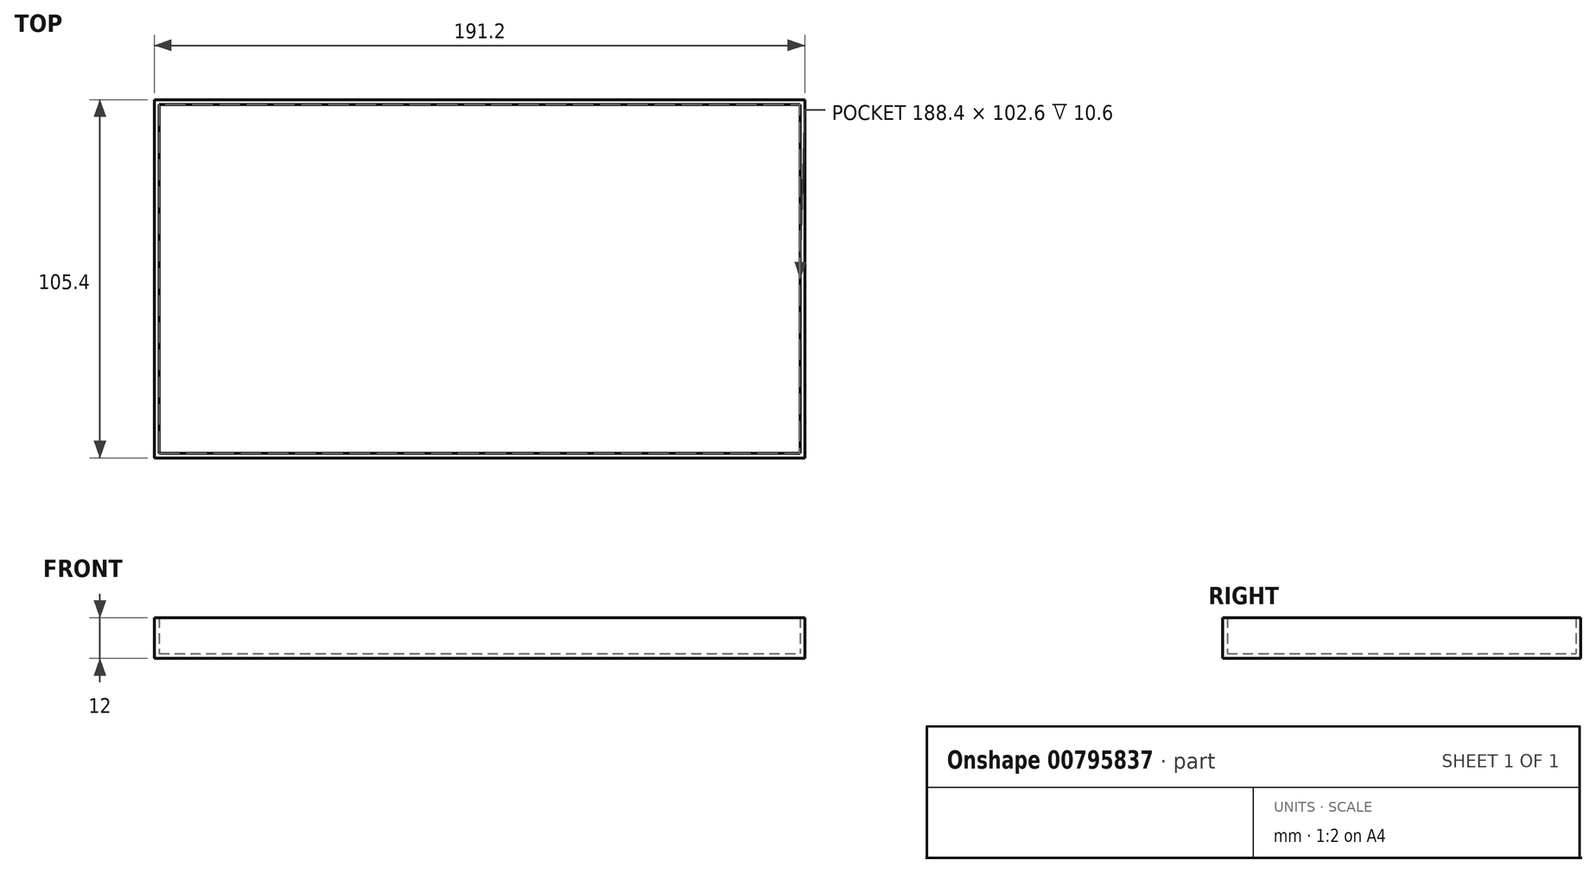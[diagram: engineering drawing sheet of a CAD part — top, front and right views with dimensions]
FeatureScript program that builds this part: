
annotation { "Feature Type Name" : "Feature", "Feature Type Description" : "" }
export const myFeature = defineFeature(function(context is Context, id is Id, definition is map)
    precondition{}
    {
        {
            var Q0;
            Q0=qCreatedBy(makeId("Top.planeOp"),FACE);
            var sketch = newSketch(context, id + "F0", { "sketchPlane" : qUnion([Q0]) });
            skLineSegment(sketch, "E0", {"start": v(-112.85, 61.36) * mm, "end": v(78.35, 61.36) * mm});
            skLineSegment(sketch, "E1", {"start": v(78.35, 61.36) * mm, "end": v(78.35, -44.04) * mm});
            skLineSegment(sketch, "E2", {"start": v(78.35, -44.04) * mm, "end": v(-112.85, -44.04) * mm});
            skLineSegment(sketch, "E3", {"start": v(-112.85, -44.04) * mm, "end": v(-112.85, 61.36) * mm});
            skSolve(sketch);
        }
        {
            var Q0;
            Q0 = qSketchRegion(id + "F0", true);
            extrude(context, id + "F1", {"entities" : qUnion([Q0]), "depth" : 12 * mm, "offsetDistance" : 25 * mm});
        }
        {
            var Q0;
            Q0=makeQuery(id+"F1.opExtrude","CAP_FACE",FACE,{"disambiguationData":[OSD([sQuery(id+"F0.wireOp",EDGE,"E0"),sQuery(id+"F0.wireOp",EDGE,"E1"),sQuery(id+"F0.wireOp",EDGE,"E2"),sQuery(id+"F0.wireOp",EDGE,"E3")])],"isStart":false});
            shell(context, id + "F2", {"entities" : qUnion([Q0]), "thickness" : 1.4 * mm});
        }
    });
